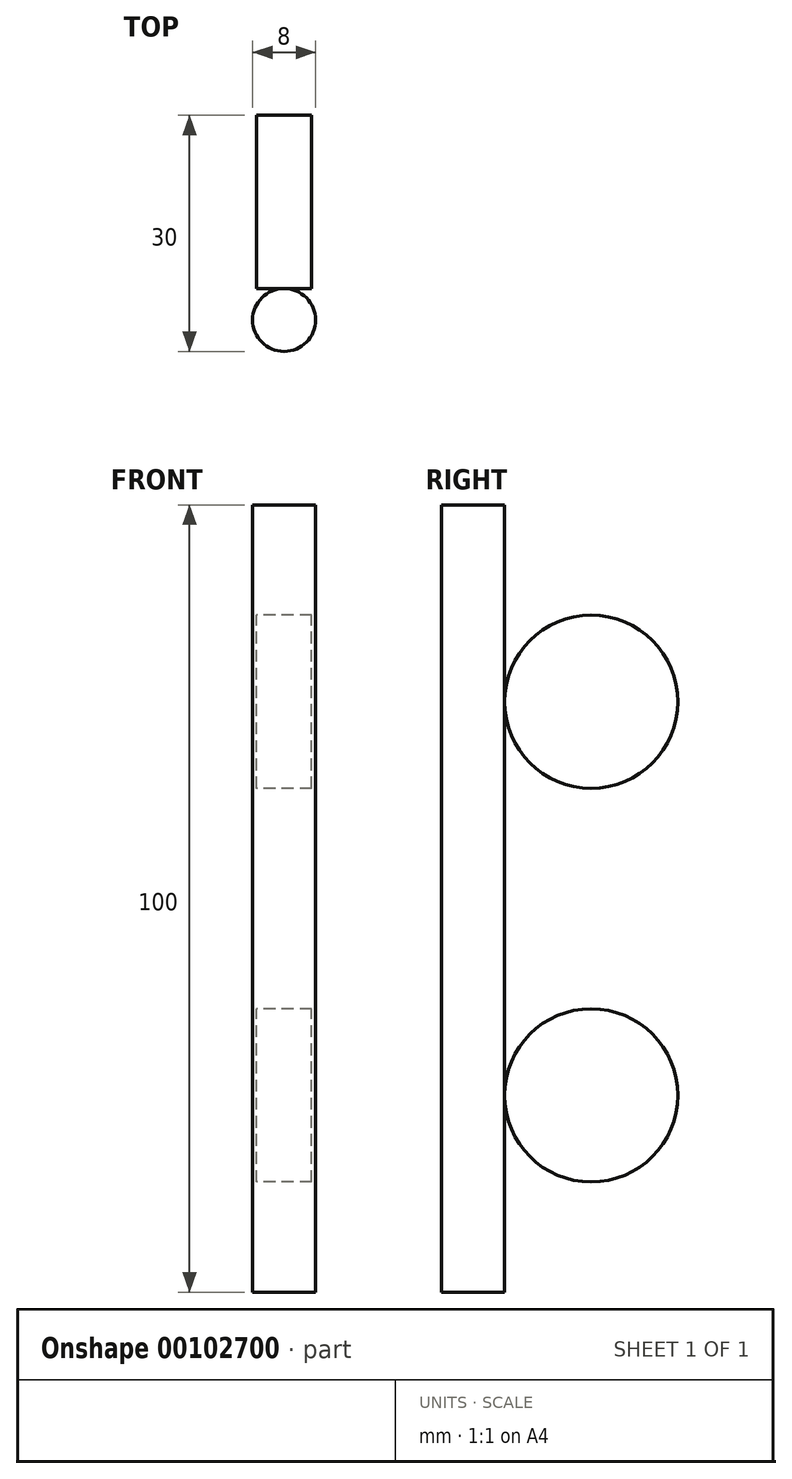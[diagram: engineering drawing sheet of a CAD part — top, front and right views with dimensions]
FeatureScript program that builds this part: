
annotation { "Feature Type Name" : "Feature", "Feature Type Description" : "" }
export const myFeature = defineFeature(function(context is Context, id is Id, definition is map)
    precondition{}
    {
        {
            var Q0;
            Q0=qCreatedBy(makeId("Top.planeOp"),FACE);
            var sketch = newSketch(context, id + "F0", { "sketchPlane" : qUnion([Q0])});
            skCircle(sketch, "E0", {"center": v(0, 0) * mm, "radius": 4 * mm});
            skSolve(sketch);
        }
        {
            var Q0;
            Q0 = qSketchRegion(id + "F0", true);
            extrude(context, id + "F1", {"entities" : qUnion([Q0]), "endBound" : BoundingType.SYMMETRIC, "depth" : 100 * mm});
        }
        {
            var Q0;
            Q0=qCreatedBy(makeId("Top.planeOp"),FACE);
            var sketch = newSketch(context, id + "F2", { "sketchPlane" : qUnion([Q0])});
            skLineSegment(sketch, "E1", {"start": v(0, 0) * mm, "end": v(0, 52.83) * mm, "construction": true});
            skLineSegment(sketch, "E2.1.0", {"start": v(0, 0) * mm, "end": v(-45.76, -26.42) * mm, "construction": true});
            skLineSegment(sketch, "E2.2.0", {"start": v(0, 0) * mm, "end": v(45.76, -26.42) * mm, "construction": true});
            skPoint(sketch, "E2.center", {"position": v(0, 0) * mm});
            skSolve(sketch);
        }
        {
            var Q0;
            Q0=qCreatedBy(makeId("Right.planeOp"),FACE);
            var sketch = newSketch(context, id + "F3", { "sketchPlane" : qUnion([Q0])});
            skCircle(sketch, "E3", {"center": v(15, 25) * mm, "radius": 11 * mm});
            skLineSegment(sketch, "E4", {"start": v(4, 50) * mm, "end": v(4, -50) * mm, "construction": true});
            skCircle(sketch, "E5.MirrorC", {"center": v(15, -25) * mm, "radius": 11 * mm});
            skSolve(sketch);
        }
        {
            var Q0;
            Q0 = qSketchRegion(id + "F3", true);
            extrude(context, id + "F4", {"entities" : qUnion([Q0]), "endBound" : BoundingType.SYMMETRIC, "depth" : 7 * mm});
        }
    });
